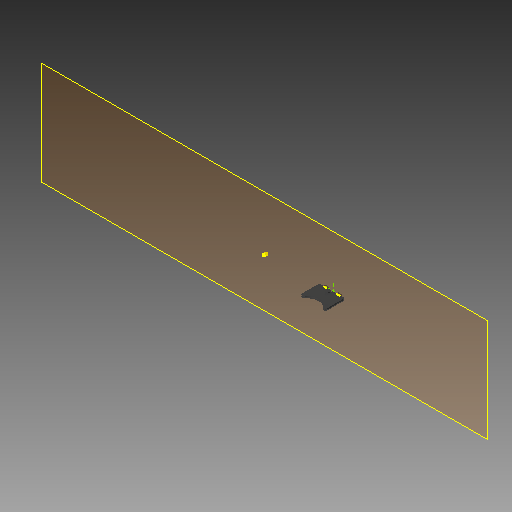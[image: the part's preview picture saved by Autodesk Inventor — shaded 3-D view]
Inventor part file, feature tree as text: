
AUTODESK INVENTOR PART (.ipt)
format: ipt  version: 2017 (Build 210142000, 142)  size: 184,320 bytes
history: native  units: mm
features: sketch x7, extrude x6, fillet x2, reference x2, projected_geometry x2, other x2, plane x1
ambient origin geometry x8: Origin, YZ Plane, XZ Plane, XY Plane, X Axis, Y Axis, Z Axis, Center Point
bodies: Solid1 (feature_tree)
feature tree (22):
  plane  "Work Plane1"
  extrude  "Extrusion1"  Depth=3.0mm
  sketch  "Sketch2"  dims[d2=6.0mm d3=3.0mm]
  extrude  "Extrusion2"  Depth=3.0mm
  extrude  "Extrusion3"  Depth=40.0mm
  fillet  "Fillet1"  Radius=3.0mm
  extrude  "Extrusion4"  Depth=40.0mm
  fillet  "Fillet2"  Radius=38.0mm
  extrude  "Extrusion5"  Depth=16.0mm
  sketch  "Sketch7"  dims[d17=2.0mm d18=40.0mm d19=0.0mm d20=2.0mm d21=1.5mm d22=10.7mm d23=1.5mm d24=6.0mm d25=1.2mm d26=2.0mm d27=40.0mm d28=0.0mm]
  sketch  "Sketch1"  dims[d0=6.0mm d1=3.0mm]
  reference  "Reference1"
  reference  "Reference2"
  projected_geometry  "Projected Loop1"
  projected_geometry  "Projected Loop2"
  sketch  "Sketch3"  dims[d4=3.0mm d5=0.0mm d6=40.0mm d7=3.0mm]
  sketch  "Sketch4"  dims[d8=60.0mm d9=0.0mm d10=40.0mm d11=38.0mm]
  sketch  "Sketch5"  dims[d12=16.0mm d13=16.0mm]
  sketch  "Sketch6"  dims[d14=3.2mm d15=40.0mm d16=0.0mm]
  other  "<userpath>\OneDrive\Inventor\Beast 3D Printer\Extruder Assembly.iam"
  extrude  "Extruder Assembly.iam"  Depth=40.0mm TaperAngle=0.0deg
  other  "Rear Extruder Panel:1"
